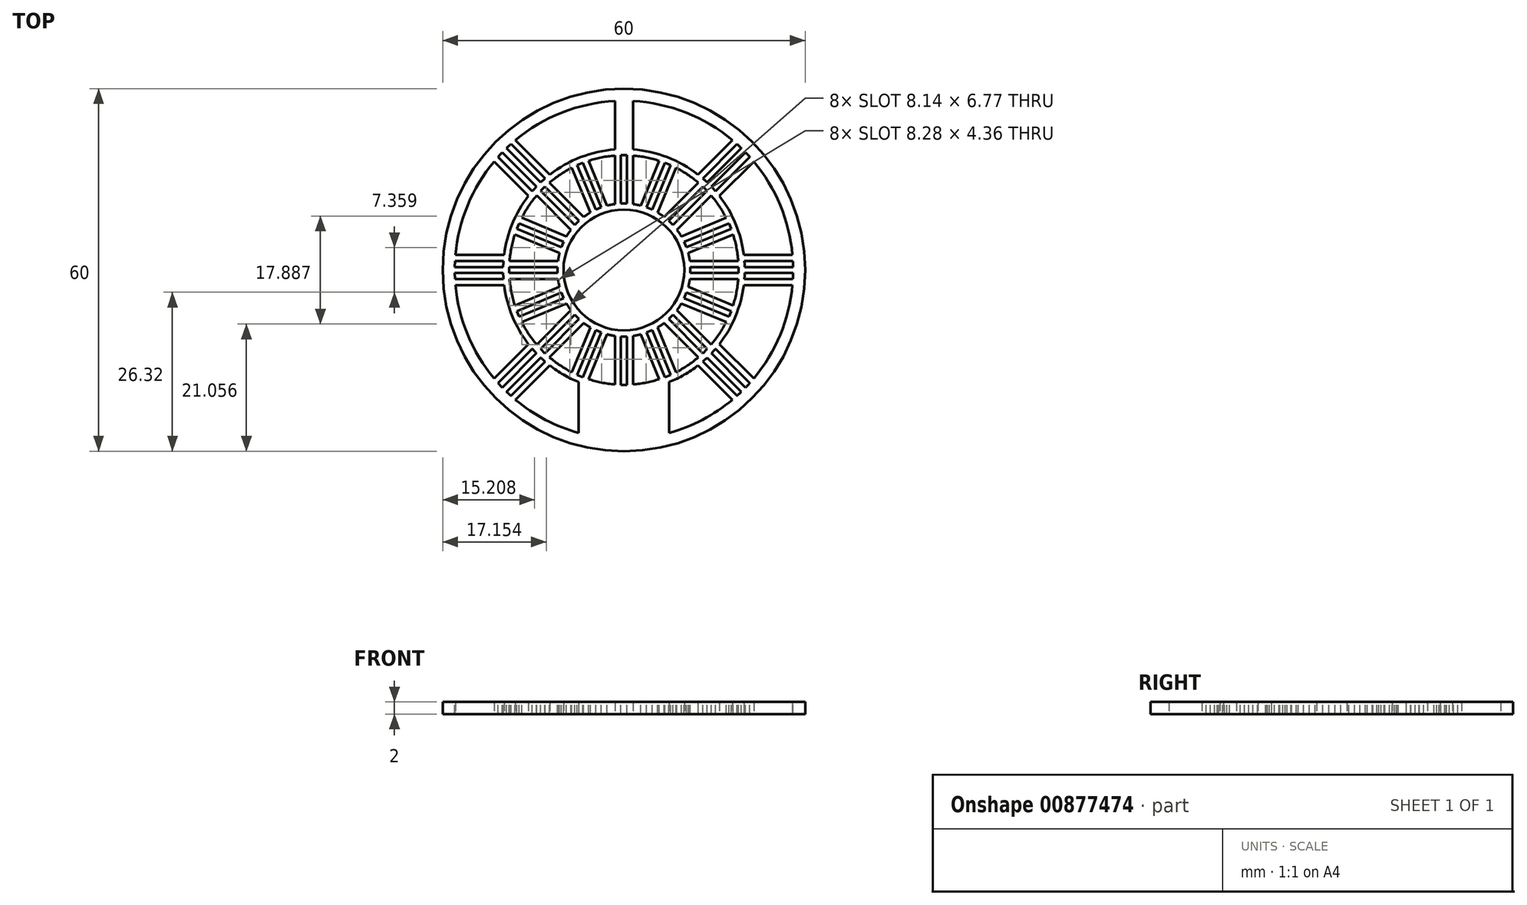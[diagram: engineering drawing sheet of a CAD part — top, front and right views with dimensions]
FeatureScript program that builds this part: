
annotation { "Feature Type Name" : "Feature", "Feature Type Description" : "" }
export const myFeature = defineFeature(function(context is Context, id is Id, definition is map)
    precondition{}
    {
        {
            var Q0;
            Q0=qCreatedBy(makeId("Top.planeOp"),FACE);
            var sketch = newSketch(context, id + "F0", { "sketchPlane" : qUnion([Q0])});
            skLineSegment(sketch, "E0", {"start": v(0, 41.56) * mm, "end": v(0, -42.56) * mm, "construction": true});
            skLineSegment(sketch, "E1", {"start": v(-1.5, 29.96) * mm, "end": v(-1.5, 19.94) * mm});
            skLineSegment(sketch, "E2.MirrorCS", {"start": v(1.5, 29.96) * mm, "end": v(1.5, 19.94) * mm});
            skCircle(sketch, "E3", {"center": v(0, 0) * mm, "radius": 10 * mm});
            skArc(sketch, "E4.trimOffspring", {"start": v(0, 30) * mm, "mid": v(-0.75, 30) * mm, "end": v(-1.5, 29.96) * mm});
            skArc(sketch, "E5", {"start": v(-1.5, 19.94) * mm, "mid": v(-7.19, 18.66) * mm, "end": v(-12.26, 15.8) * mm});
            skArc(sketch, "E6.trimOffspring", {"start": v(7.5, -18.54) * mm, "mid": v(9.98, -17.33) * mm, "end": v(12.26, -15.8) * mm});
            skLineSegment(sketch, "E7", {"start": v(-43.12, 0) * mm, "end": v(49.9, 0) * mm, "construction": true});
            skArc(sketch, "E8.trimOffspring", {"start": v(-19.6, -4) * mm, "mid": v(-18.17, -8.35) * mm, "end": v(-15.8, -12.26) * mm});
            skArc(sketch, "E9.trimOffspring", {"start": v(19.6, 4) * mm, "mid": v(18.17, 8.35) * mm, "end": v(15.8, 12.26) * mm});
            skArc(sketch, "E10", {"start": v(-19.6, 4) * mm, "mid": v(-19.73, 3.25) * mm, "end": v(-19.84, 2.5) * mm});
            skArc(sketch, "E11.trimOffspring", {"start": v(19.6, -4) * mm, "mid": v(19.73, -3.25) * mm, "end": v(19.84, -2.5) * mm});
            skLineSegment(sketch, "E12", {"start": v(-19.84, 2.5) * mm, "end": v(-29.9, 2.5) * mm});
            skLineSegment(sketch, "E13", {"start": v(-19.84, -2.5) * mm, "end": v(-29.9, -2.5) * mm});
            skArc(sketch, "E14.trimOffspring", {"start": v(-19.84, -2.5) * mm, "mid": v(-19.73, -3.25) * mm, "end": v(-19.6, -4) * mm});
            skLineSegment(sketch, "E15.MirrorCS", {"start": v(19.84, 2.5) * mm, "end": v(29.9, 2.5) * mm});
            skLineSegment(sketch, "E16.MirrorCS", {"start": v(19.84, -2.5) * mm, "end": v(29.9, -2.5) * mm});
            skArc(sketch, "E17.trimOffspring", {"start": v(19.84, 2.5) * mm, "mid": v(19.73, 3.25) * mm, "end": v(19.6, 4) * mm});
            skLineSegment(sketch, "E18", {"start": v(-7.5, -18.54) * mm, "end": v(-7.5, -29.05) * mm});
            skLineSegment(sketch, "E19", {"start": v(7.5, -18.54) * mm, "end": v(7.5, -29.05) * mm});
            skArc(sketch, "E20.trimOffspring", {"start": v(1.5, 29.96) * mm, "mid": v(0.75, 30) * mm, "end": v(0, 30) * mm});
            skPoint(sketch, "E21.orphan", {"position": v(29.9, 2.5) * mm});
            skPoint(sketch, "E22.MirrorCS.end.orphan", {"position": v(29.9, -2.5) * mm});
            skArc(sketch, "E23", {"start": v(-19.37, 22.9) * mm, "mid": v(-21.21, 21.21) * mm, "end": v(-22.9, 19.37) * mm});
            skLineSegment(sketch, "E24", {"start": v(-23.88, 23.88) * mm, "end": v(0, 0) * mm, "construction": true});
            skLineSegment(sketch, "E25", {"start": v(-12.26, 15.8) * mm, "end": v(-19.37, 22.9) * mm});
            skLineSegment(sketch, "E26", {"start": v(-15.8, 12.26) * mm, "end": v(-22.9, 19.37) * mm});
            skArc(sketch, "E27.trimOffspring", {"start": v(-29.9, 2.5) * mm, "mid": v(-30, 0) * mm, "end": v(-29.9, -2.5) * mm});
            skArc(sketch, "E28.trimOffspring", {"start": v(-7.5, -29.05) * mm, "mid": v(0, -30) * mm, "end": v(7.5, -29.05) * mm});
            skArc(sketch, "E29.trimOffspring", {"start": v(29.9, -2.5) * mm, "mid": v(30, 0) * mm, "end": v(29.9, 2.5) * mm});
            skArc(sketch, "E30.trimOffspring", {"start": v(1.5, 29.96) * mm, "mid": v(0, 30) * mm, "end": v(-1.5, 29.96) * mm});
            skArc(sketch, "E31.trimOffspring", {"start": v(-15.8, 12.26) * mm, "mid": v(-18.17, 8.35) * mm, "end": v(-19.6, 4) * mm});
            skLineSegment(sketch, "E32.MirrorCS", {"start": v(-15.8, -12.26) * mm, "end": v(-22.9, -19.37) * mm});
            skLineSegment(sketch, "E33.MirrorCS", {"start": v(-12.26, -15.8) * mm, "end": v(-19.37, -22.9) * mm});
            skArc(sketch, "E34.MirrorCS", {"start": v(-19.37, -22.9) * mm, "mid": v(-21.21, -21.21) * mm, "end": v(-22.9, -19.37) * mm});
            skArc(sketch, "E35.MirrorCS", {"start": v(19.37, 22.9) * mm, "mid": v(21.21, 21.21) * mm, "end": v(22.9, 19.37) * mm});
            skLineSegment(sketch, "E36.MirrorCS", {"start": v(12.26, 15.8) * mm, "end": v(19.37, 22.9) * mm});
            skLineSegment(sketch, "E37.MirrorCS", {"start": v(15.8, 12.26) * mm, "end": v(22.9, 19.37) * mm});
            skLineSegment(sketch, "E38.MirrorCS", {"start": v(15.8, -12.26) * mm, "end": v(22.9, -19.37) * mm});
            skArc(sketch, "E39.MirrorCS", {"start": v(19.37, -22.9) * mm, "mid": v(21.21, -21.21) * mm, "end": v(22.9, -19.37) * mm});
            skLineSegment(sketch, "E40.MirrorCS", {"start": v(12.26, -15.8) * mm, "end": v(19.37, -22.9) * mm});
            skArc(sketch, "E41.trimOffspring", {"start": v(12.26, 15.8) * mm, "mid": v(7.19, 18.66) * mm, "end": v(1.5, 19.94) * mm});
            skArc(sketch, "E42.trimOffspring", {"start": v(15.8, -12.26) * mm, "mid": v(18.17, -8.35) * mm, "end": v(19.6, -4) * mm});
            skArc(sketch, "E43.trimOffspring", {"start": v(-12.26, -15.8) * mm, "mid": v(-9.98, -17.33) * mm, "end": v(-7.5, -18.54) * mm});
            skSolve(sketch);
        }
        {
            var Q0;
            Q0=qSketchRegion(id+"F0",true);
            extrude(context, id + "F1", {"entities" : qUnion([Q0]), "depth" : 2 * mm, "offsetDistance" : 25 * mm});
        }
        {
            var Q0;
            Q0=makeQuery(id+"F1.opExtrude","CAP_FACE",FACE,{"disambiguationData":[OSD([sQuery(id+"F0.wireOp",EDGE,"E1"),sQuery(id+"F0.wireOp",EDGE,"E2.MirrorCS"),sQuery(id+"F0.wireOp",EDGE,"AAyOunAg-4wrl-KSGf-zJpX-W6BoPU9CkmaY"),sQuery(id+"F0.wireOp",EDGE,"E3"),sQuery(id+"F0.wireOp",EDGE,"E4.trimOffspring"),sQuery(id+"F0.wireOp",EDGE,"E5"),sQuery(id+"F0.wireOp",EDGE,"c113f9d6-7eb6-46a0-945d-8de39da3101e.trimOffspring"),sQuery(id+"F0.wireOp",EDGE,"3f556c1b-9434-4d6c-9e8b-53cfe23b14e8.trimOffspring"),sQuery(id+"F0.wireOp",EDGE,"E6.trimOffspring"),sQuery(id+"F0.wireOp",EDGE,"E8.trimOffspring"),sQuery(id+"F0.wireOp",EDGE,"E9.trimOffspring"),sQuery(id+"F0.wireOp",EDGE,"E10"),sQuery(id+"F0.wireOp",EDGE,"E11.trimOffspring")])],"isStart":false});
            var sketch = newSketch(context, id + "F2", { "sketchPlane" : qUnion([Q0])});
            skLineSegment(sketch, "E44", {"start": v(0, 19.87) * mm, "end": v(0, -17.42) * mm, "construction": true});
            skLineSegment(sketch, "E45", {"start": v(-0.5, 19) * mm, "end": v(-0.5, 11) * mm});
            skLineSegment(sketch, "E46", {"start": v(-0.5, 11) * mm, "end": v(0, 11) * mm});
            skLineSegment(sketch, "E47", {"start": v(-0.5, 19) * mm, "end": v(0, 19) * mm});
            skCircle(sketch, "E48", {"center": v(0, 0) * mm, "radius": 15 * mm, "construction": true});
            skLineSegment(sketch, "E49.MirrorCS", {"start": v(0.5, 19) * mm, "end": v(0, 19) * mm});
            skLineSegment(sketch, "E50.MirrorCS", {"start": v(0.5, 19) * mm, "end": v(0.5, 11) * mm});
            skLineSegment(sketch, "E51.MirrorCS", {"start": v(0.5, 11) * mm, "end": v(0, 11) * mm});
            skLineSegment(sketch, "E52.1.0", {"start": v(7.73, 17.36) * mm, "end": v(7.27, 17.55) * mm});
            skLineSegment(sketch, "E52.1.1", {"start": v(7.73, 17.36) * mm, "end": v(4.67, 9.97) * mm});
            skLineSegment(sketch, "E52.1.2", {"start": v(6.8, 17.75) * mm, "end": v(7.27, 17.55) * mm});
            skLineSegment(sketch, "E52.1.3", {"start": v(6.8, 17.75) * mm, "end": v(3.75, 10.35) * mm});
            skLineSegment(sketch, "E52.1.4", {"start": v(3.75, 10.35) * mm, "end": v(4.2, 10.16) * mm});
            skLineSegment(sketch, "E52.1.5", {"start": v(4.67, 9.97) * mm, "end": v(4.2, 10.16) * mm});
            skLineSegment(sketch, "E52.2.0", {"start": v(13.79, 13.08) * mm, "end": v(13.44, 13.44) * mm});
            skLineSegment(sketch, "E52.2.1", {"start": v(13.79, 13.08) * mm, "end": v(8.13, 7.42) * mm});
            skLineSegment(sketch, "E52.2.2", {"start": v(13.08, 13.79) * mm, "end": v(13.44, 13.44) * mm});
            skLineSegment(sketch, "E52.2.3", {"start": v(13.08, 13.79) * mm, "end": v(7.42, 8.13) * mm});
            skLineSegment(sketch, "E52.2.4", {"start": v(7.42, 8.13) * mm, "end": v(7.78, 7.78) * mm});
            skLineSegment(sketch, "E52.2.5", {"start": v(8.13, 7.42) * mm, "end": v(7.78, 7.78) * mm});
            skLineSegment(sketch, "E52.3.0", {"start": v(17.75, 6.8) * mm, "end": v(17.55, 7.27) * mm});
            skLineSegment(sketch, "E52.3.1", {"start": v(17.75, 6.8) * mm, "end": v(10.35, 3.75) * mm});
            skLineSegment(sketch, "E52.3.2", {"start": v(17.36, 7.73) * mm, "end": v(17.55, 7.27) * mm});
            skLineSegment(sketch, "E52.3.3", {"start": v(17.36, 7.73) * mm, "end": v(9.97, 4.67) * mm});
            skLineSegment(sketch, "E52.3.4", {"start": v(9.97, 4.67) * mm, "end": v(10.16, 4.2) * mm});
            skLineSegment(sketch, "E52.3.5", {"start": v(10.35, 3.75) * mm, "end": v(10.16, 4.2) * mm});
            skLineSegment(sketch, "E52.4.0", {"start": v(19, -0.5) * mm, "end": v(19, 0) * mm});
            skLineSegment(sketch, "E52.4.1", {"start": v(19, -0.5) * mm, "end": v(11, -0.5) * mm});
            skLineSegment(sketch, "E52.4.2", {"start": v(19, 0.5) * mm, "end": v(19, 0) * mm});
            skLineSegment(sketch, "E52.4.3", {"start": v(19, 0.5) * mm, "end": v(11, 0.5) * mm});
            skLineSegment(sketch, "E52.4.4", {"start": v(11, 0.5) * mm, "end": v(11, 0) * mm});
            skLineSegment(sketch, "E52.4.5", {"start": v(11, -0.5) * mm, "end": v(11, 0) * mm});
            skLineSegment(sketch, "E52.5.0", {"start": v(17.36, -7.73) * mm, "end": v(17.55, -7.27) * mm});
            skLineSegment(sketch, "E52.5.1", {"start": v(17.36, -7.73) * mm, "end": v(9.97, -4.67) * mm});
            skLineSegment(sketch, "E52.5.2", {"start": v(17.75, -6.8) * mm, "end": v(17.55, -7.27) * mm});
            skLineSegment(sketch, "E52.5.3", {"start": v(17.75, -6.8) * mm, "end": v(10.35, -3.75) * mm});
            skLineSegment(sketch, "E52.5.4", {"start": v(10.35, -3.75) * mm, "end": v(10.16, -4.2) * mm});
            skLineSegment(sketch, "E52.5.5", {"start": v(9.97, -4.67) * mm, "end": v(10.16, -4.2) * mm});
            skLineSegment(sketch, "E52.6.0", {"start": v(13.08, -13.79) * mm, "end": v(13.44, -13.44) * mm});
            skLineSegment(sketch, "E52.6.1", {"start": v(13.08, -13.79) * mm, "end": v(7.42, -8.13) * mm});
            skLineSegment(sketch, "E52.6.2", {"start": v(13.79, -13.08) * mm, "end": v(13.44, -13.44) * mm});
            skLineSegment(sketch, "E52.6.3", {"start": v(13.79, -13.08) * mm, "end": v(8.13, -7.42) * mm});
            skLineSegment(sketch, "E52.6.4", {"start": v(8.13, -7.42) * mm, "end": v(7.78, -7.78) * mm});
            skLineSegment(sketch, "E52.6.5", {"start": v(7.42, -8.13) * mm, "end": v(7.78, -7.78) * mm});
            skLineSegment(sketch, "E52.7.0", {"start": v(6.8, -17.75) * mm, "end": v(7.27, -17.55) * mm});
            skLineSegment(sketch, "E52.7.1", {"start": v(6.8, -17.75) * mm, "end": v(3.75, -10.35) * mm});
            skLineSegment(sketch, "E52.7.2", {"start": v(7.73, -17.36) * mm, "end": v(7.27, -17.55) * mm});
            skLineSegment(sketch, "E52.7.3", {"start": v(7.73, -17.36) * mm, "end": v(4.67, -9.97) * mm});
            skLineSegment(sketch, "E52.7.4", {"start": v(4.67, -9.97) * mm, "end": v(4.2, -10.16) * mm});
            skLineSegment(sketch, "E52.7.5", {"start": v(3.75, -10.35) * mm, "end": v(4.2, -10.16) * mm});
            skLineSegment(sketch, "E52.8.0", {"start": v(-0.5, -19) * mm, "end": v(0, -19) * mm});
            skLineSegment(sketch, "E52.8.1", {"start": v(-0.5, -19) * mm, "end": v(-0.5, -11) * mm});
            skLineSegment(sketch, "E52.8.2", {"start": v(0.5, -19) * mm, "end": v(0, -19) * mm});
            skLineSegment(sketch, "E52.8.3", {"start": v(0.5, -19) * mm, "end": v(0.5, -11) * mm});
            skLineSegment(sketch, "E52.8.4", {"start": v(0.5, -11) * mm, "end": v(0, -11) * mm});
            skLineSegment(sketch, "E52.8.5", {"start": v(-0.5, -11) * mm, "end": v(0, -11) * mm});
            skLineSegment(sketch, "E52.anchor1", {"start": v(0, 0) * mm, "end": v(0, 19) * mm, "construction": true});
            skLineSegment(sketch, "E52.anchor2", {"start": v(0, 0) * mm, "end": v(0, -19) * mm, "construction": true});
            skLineSegment(sketch, "E53.MirrorCS", {"start": v(-13.79, 13.08) * mm, "end": v(-13.44, 13.44) * mm});
            skLineSegment(sketch, "E54.MirrorCS", {"start": v(-19, 0.5) * mm, "end": v(-19, 0) * mm});
            skLineSegment(sketch, "E55.MirrorCS", {"start": v(-7.42, 8.13) * mm, "end": v(-7.78, 7.78) * mm});
            skLineSegment(sketch, "E56.MirrorCS", {"start": v(-17.75, -6.8) * mm, "end": v(-17.55, -7.27) * mm});
            skLineSegment(sketch, "E57.MirrorCS", {"start": v(-13.08, 13.79) * mm, "end": v(-13.44, 13.44) * mm});
            skLineSegment(sketch, "E58.MirrorCS", {"start": v(-8.13, -7.42) * mm, "end": v(-7.78, -7.78) * mm});
            skLineSegment(sketch, "E59.MirrorCS", {"start": v(-13.79, -13.08) * mm, "end": v(-13.44, -13.44) * mm});
            skLineSegment(sketch, "E60.MirrorCS", {"start": v(-17.75, 6.8) * mm, "end": v(-17.55, 7.27) * mm});
            skLineSegment(sketch, "E61.MirrorCS", {"start": v(-19, -0.5) * mm, "end": v(-19, 0) * mm});
            skLineSegment(sketch, "E62.MirrorCS", {"start": v(-13.08, -13.79) * mm, "end": v(-13.44, -13.44) * mm});
            skLineSegment(sketch, "E63.MirrorCS", {"start": v(-11, 0.5) * mm, "end": v(-11, 0) * mm});
            skLineSegment(sketch, "E64.MirrorCS", {"start": v(-6.8, -17.75) * mm, "end": v(-7.27, -17.55) * mm});
            skLineSegment(sketch, "E65.MirrorCS", {"start": v(-10.35, -3.75) * mm, "end": v(-10.16, -4.2) * mm});
            skLineSegment(sketch, "E66.MirrorCS", {"start": v(-7.73, 17.36) * mm, "end": v(-7.27, 17.55) * mm});
            skLineSegment(sketch, "E67.MirrorCS", {"start": v(-9.97, 4.67) * mm, "end": v(-10.16, 4.2) * mm});
            skLineSegment(sketch, "E68.MirrorCS", {"start": v(-9.97, -4.67) * mm, "end": v(-10.16, -4.2) * mm});
            skLineSegment(sketch, "E69.MirrorCS", {"start": v(-10.35, 3.75) * mm, "end": v(-10.16, 4.2) * mm});
            skLineSegment(sketch, "E70.MirrorCS", {"start": v(-7.73, -17.36) * mm, "end": v(-7.27, -17.55) * mm});
            skLineSegment(sketch, "E71.MirrorCS", {"start": v(-8.13, 7.42) * mm, "end": v(-7.78, 7.78) * mm});
            skLineSegment(sketch, "E72.MirrorCS", {"start": v(-7.42, -8.13) * mm, "end": v(-7.78, -7.78) * mm});
            skLineSegment(sketch, "E73.MirrorCS", {"start": v(-17.36, 7.73) * mm, "end": v(-17.55, 7.27) * mm});
            skLineSegment(sketch, "E74.MirrorCS", {"start": v(-11, -0.5) * mm, "end": v(-11, 0) * mm});
            skLineSegment(sketch, "E75.MirrorCS", {"start": v(-6.8, 17.75) * mm, "end": v(-7.27, 17.55) * mm});
            skLineSegment(sketch, "E76.MirrorCS", {"start": v(-17.36, -7.73) * mm, "end": v(-17.55, -7.27) * mm});
            skLineSegment(sketch, "E77.MirrorCS", {"start": v(-17.36, 7.73) * mm, "end": v(-9.97, 4.67) * mm});
            skLineSegment(sketch, "E78.MirrorCS", {"start": v(-13.79, -13.08) * mm, "end": v(-8.13, -7.42) * mm});
            skLineSegment(sketch, "E79.MirrorCS", {"start": v(-17.75, -6.8) * mm, "end": v(-10.35, -3.75) * mm});
            skLineSegment(sketch, "E80.MirrorCS", {"start": v(-19, 0.5) * mm, "end": v(-11, 0.5) * mm});
            skLineSegment(sketch, "E81.MirrorCS", {"start": v(-7.73, -17.36) * mm, "end": v(-4.67, -9.97) * mm});
            skLineSegment(sketch, "E82.MirrorCS", {"start": v(-17.75, 6.8) * mm, "end": v(-10.35, 3.75) * mm});
            skLineSegment(sketch, "E83.MirrorCS", {"start": v(-17.36, -7.73) * mm, "end": v(-9.97, -4.67) * mm});
            skLineSegment(sketch, "E84.MirrorCS", {"start": v(-7.73, 17.36) * mm, "end": v(-4.67, 9.97) * mm});
            skLineSegment(sketch, "E85.MirrorCS", {"start": v(-13.08, 13.79) * mm, "end": v(-7.42, 8.13) * mm});
            skLineSegment(sketch, "E86.MirrorCS", {"start": v(-19, -0.5) * mm, "end": v(-11, -0.5) * mm});
            skLineSegment(sketch, "E87.MirrorCS", {"start": v(-13.79, 13.08) * mm, "end": v(-8.13, 7.42) * mm});
            skLineSegment(sketch, "E88.MirrorCS", {"start": v(-13.08, -13.79) * mm, "end": v(-7.42, -8.13) * mm});
            skLineSegment(sketch, "E89.MirrorCS", {"start": v(-6.8, 17.75) * mm, "end": v(-3.75, 10.35) * mm});
            skLineSegment(sketch, "E90.MirrorCS", {"start": v(-3.75, 10.35) * mm, "end": v(-4.2, 10.16) * mm});
            skLineSegment(sketch, "E91.MirrorCS", {"start": v(-4.67, 9.97) * mm, "end": v(-4.2, 10.16) * mm});
            skLineSegment(sketch, "E92.MirrorCS", {"start": v(-3.75, -10.35) * mm, "end": v(-4.2, -10.16) * mm});
            skLineSegment(sketch, "E93.MirrorCS", {"start": v(-4.67, -9.97) * mm, "end": v(-4.2, -10.16) * mm});
            skLineSegment(sketch, "E94.MirrorCS", {"start": v(-6.8, -17.75) * mm, "end": v(-3.75, -10.35) * mm});
            skSolve(sketch);
        }
        {
            var Q0;
            Q0=qSketchRegion(id+"F2",true);
            extrude(context, id + "F3", {"entities" : qUnion([Q0]), "operationType" : NewBodyOperationType.REMOVE, "oppositeDirection" : true, "depth" : 25 * mm, "offsetDistance" : 25 * mm});
        }
        {
            var Q0;
            Q0=makeQuery(id+"F1.opExtrude","CAP_FACE",FACE,{"disambiguationData":[OSD([sQuery(id+"F0.wireOp",EDGE,"E1"),sQuery(id+"F0.wireOp",EDGE,"E2.MirrorCS"),sQuery(id+"F0.wireOp",EDGE,"AAyOunAg-4wrl-KSGf-zJpX-W6BoPU9CkmaY"),sQuery(id+"F0.wireOp",EDGE,"E3"),sQuery(id+"F0.wireOp",EDGE,"E4.trimOffspring"),sQuery(id+"F0.wireOp",EDGE,"E5"),sQuery(id+"F0.wireOp",EDGE,"c113f9d6-7eb6-46a0-945d-8de39da3101e.trimOffspring"),sQuery(id+"F0.wireOp",EDGE,"3f556c1b-9434-4d6c-9e8b-53cfe23b14e8.trimOffspring"),sQuery(id+"F0.wireOp",EDGE,"E6.trimOffspring"),sQuery(id+"F0.wireOp",EDGE,"E8.trimOffspring"),sQuery(id+"F0.wireOp",EDGE,"E9.trimOffspring"),sQuery(id+"F0.wireOp",EDGE,"E10"),sQuery(id+"F0.wireOp",EDGE,"E11.trimOffspring")])],"isStart":false});
            var sketch = newSketch(context, id + "F4", { "sketchPlane" : qUnion([Q0])});
            skArc(sketch, "E95", {"start": v(-1.5, 10.9) * mm, "mid": v(-2.15, 10.8) * mm, "end": v(-2.79, 10.65) * mm});
            skLineSegment(sketch, "E96", {"start": v(-1.5, 10.9) * mm, "end": v(-1.5, 18.93) * mm});
            skLineSegment(sketch, "E97", {"start": v(-2.79, 10.65) * mm, "end": v(-5.86, 18.07) * mm});
            skArc(sketch, "E98", {"start": v(-1.5, 18.93) * mm, "mid": v(-3.7, 18.63) * mm, "end": v(-5.86, 18.07) * mm});
            skArc(sketch, "E99.1.0", {"start": v(5.86, 18.07) * mm, "mid": v(3.7, 18.63) * mm, "end": v(1.5, 18.93) * mm});
            skLineSegment(sketch, "E99.1.1", {"start": v(2.79, 10.65) * mm, "end": v(5.86, 18.07) * mm});
            skArc(sketch, "E99.1.2", {"start": v(2.79, 10.65) * mm, "mid": v(2.15, 10.8) * mm, "end": v(1.5, 10.9) * mm});
            skLineSegment(sketch, "E99.1.3", {"start": v(1.5, 10.9) * mm, "end": v(1.5, 18.93) * mm});
            skArc(sketch, "E99.2.0", {"start": v(12.33, 14.45) * mm, "mid": v(10.55, 15.8) * mm, "end": v(8.63, 16.92) * mm});
            skLineSegment(sketch, "E99.2.1", {"start": v(6.65, 8.77) * mm, "end": v(12.33, 14.45) * mm});
            skArc(sketch, "E99.2.2", {"start": v(6.65, 8.77) * mm, "mid": v(6.12, 9.16) * mm, "end": v(5.56, 9.5) * mm});
            skLineSegment(sketch, "E99.2.3", {"start": v(5.56, 9.5) * mm, "end": v(8.63, 16.92) * mm});
            skArc(sketch, "E99.3.0", {"start": v(16.92, 8.63) * mm, "mid": v(15.8, 10.55) * mm, "end": v(14.45, 12.33) * mm});
            skLineSegment(sketch, "E99.3.1", {"start": v(9.5, 5.56) * mm, "end": v(16.92, 8.63) * mm});
            skArc(sketch, "E99.3.2", {"start": v(9.5, 5.56) * mm, "mid": v(9.16, 6.12) * mm, "end": v(8.77, 6.65) * mm});
            skLineSegment(sketch, "E99.3.3", {"start": v(8.77, 6.65) * mm, "end": v(14.45, 12.33) * mm});
            skArc(sketch, "E99.4.0", {"start": v(18.93, 1.5) * mm, "mid": v(18.63, 3.7) * mm, "end": v(18.07, 5.86) * mm});
            skLineSegment(sketch, "E99.4.1", {"start": v(10.9, 1.5) * mm, "end": v(18.93, 1.5) * mm});
            skArc(sketch, "E99.4.2", {"start": v(10.9, 1.5) * mm, "mid": v(10.8, 2.15) * mm, "end": v(10.65, 2.79) * mm});
            skLineSegment(sketch, "E99.4.3", {"start": v(10.65, 2.79) * mm, "end": v(18.07, 5.86) * mm});
            skArc(sketch, "E99.5.0", {"start": v(18.07, -5.86) * mm, "mid": v(18.63, -3.7) * mm, "end": v(18.93, -1.5) * mm});
            skLineSegment(sketch, "E99.5.1", {"start": v(10.65, -2.79) * mm, "end": v(18.07, -5.86) * mm});
            skArc(sketch, "E99.5.2", {"start": v(10.65, -2.79) * mm, "mid": v(10.8, -2.15) * mm, "end": v(10.9, -1.5) * mm});
            skLineSegment(sketch, "E99.5.3", {"start": v(10.9, -1.5) * mm, "end": v(18.93, -1.5) * mm});
            skArc(sketch, "E99.6.0", {"start": v(14.45, -12.33) * mm, "mid": v(15.8, -10.55) * mm, "end": v(16.92, -8.63) * mm});
            skLineSegment(sketch, "E99.6.1", {"start": v(8.77, -6.65) * mm, "end": v(14.45, -12.33) * mm});
            skArc(sketch, "E99.6.2", {"start": v(8.77, -6.65) * mm, "mid": v(9.16, -6.12) * mm, "end": v(9.5, -5.56) * mm});
            skLineSegment(sketch, "E99.6.3", {"start": v(9.5, -5.56) * mm, "end": v(16.92, -8.63) * mm});
            skArc(sketch, "E99.7.0", {"start": v(8.63, -16.92) * mm, "mid": v(10.55, -15.8) * mm, "end": v(12.33, -14.45) * mm});
            skLineSegment(sketch, "E99.7.1", {"start": v(5.56, -9.5) * mm, "end": v(8.63, -16.92) * mm});
            skArc(sketch, "E99.7.2", {"start": v(5.56, -9.5) * mm, "mid": v(6.12, -9.16) * mm, "end": v(6.65, -8.77) * mm});
            skLineSegment(sketch, "E99.7.3", {"start": v(6.65, -8.77) * mm, "end": v(12.33, -14.45) * mm});
            skArc(sketch, "E99.8.0", {"start": v(1.5, -18.93) * mm, "mid": v(3.7, -18.63) * mm, "end": v(5.86, -18.07) * mm});
            skLineSegment(sketch, "E99.8.1", {"start": v(1.5, -10.9) * mm, "end": v(1.5, -18.93) * mm});
            skArc(sketch, "E99.8.2", {"start": v(1.5, -10.9) * mm, "mid": v(2.15, -10.8) * mm, "end": v(2.79, -10.65) * mm});
            skLineSegment(sketch, "E99.8.3", {"start": v(2.79, -10.65) * mm, "end": v(5.86, -18.07) * mm});
            skLineSegment(sketch, "E99.anchor1", {"start": v(0, 0) * mm, "end": v(-5.86, 18.07) * mm, "construction": true});
            skLineSegment(sketch, "E99.anchor2", {"start": v(0, 0) * mm, "end": v(5.86, -18.07) * mm, "construction": true});
            skLineSegment(sketch, "E100", {"start": v(0, 24.57) * mm, "end": v(0, -24.9) * mm, "construction": true});
            skPoint(sketch, "E100.startSnap0", {"position": v(0, 23.23) * mm});
            skArc(sketch, "E101.MirrorCS", {"start": v(-12.33, 14.45) * mm, "mid": v(-10.55, 15.8) * mm, "end": v(-8.63, 16.92) * mm});
            skArc(sketch, "E102.MirrorCS", {"start": v(-10.9, 1.5) * mm, "mid": v(-10.8, 2.15) * mm, "end": v(-10.65, 2.79) * mm});
            skArc(sketch, "E103.MirrorCS", {"start": v(-8.77, -6.65) * mm, "mid": v(-9.16, -6.12) * mm, "end": v(-9.5, -5.56) * mm});
            skArc(sketch, "E104.MirrorCS", {"start": v(-10.65, -2.79) * mm, "mid": v(-10.8, -2.15) * mm, "end": v(-10.9, -1.5) * mm});
            skArc(sketch, "E105.MirrorCS", {"start": v(-9.5, 5.56) * mm, "mid": v(-9.16, 6.12) * mm, "end": v(-8.77, 6.65) * mm});
            skLineSegment(sketch, "E106.MirrorCS", {"start": v(-10.9, 1.5) * mm, "end": v(-18.93, 1.5) * mm});
            skLineSegment(sketch, "E107.MirrorCS", {"start": v(-8.77, -6.65) * mm, "end": v(-14.45, -12.33) * mm});
            skLineSegment(sketch, "E108.MirrorCS", {"start": v(-9.5, -5.56) * mm, "end": v(-16.92, -8.63) * mm});
            skArc(sketch, "E109.MirrorCS", {"start": v(-8.63, -16.92) * mm, "mid": v(-10.55, -15.8) * mm, "end": v(-12.33, -14.45) * mm});
            skArc(sketch, "E110.MirrorCS", {"start": v(-16.92, 8.63) * mm, "mid": v(-15.8, 10.55) * mm, "end": v(-14.45, 12.33) * mm});
            skLineSegment(sketch, "E111.MirrorCS", {"start": v(-10.65, -2.79) * mm, "end": v(-18.07, -5.86) * mm});
            skArc(sketch, "E112.MirrorCS", {"start": v(-14.45, -12.33) * mm, "mid": v(-15.8, -10.55) * mm, "end": v(-16.92, -8.63) * mm});
            skArc(sketch, "E113.MirrorCS", {"start": v(-18.93, 1.5) * mm, "mid": v(-18.63, 3.7) * mm, "end": v(-18.07, 5.86) * mm});
            skLineSegment(sketch, "E114.MirrorCS", {"start": v(-8.77, 6.65) * mm, "end": v(-14.45, 12.33) * mm});
            skLineSegment(sketch, "E115.MirrorCS", {"start": v(-10.65, 2.79) * mm, "end": v(-18.07, 5.86) * mm});
            skLineSegment(sketch, "E116.MirrorCS", {"start": v(-10.9, -1.5) * mm, "end": v(-18.93, -1.5) * mm});
            skLineSegment(sketch, "E117.MirrorCS", {"start": v(-9.5, 5.56) * mm, "end": v(-16.92, 8.63) * mm});
            skArc(sketch, "E118.MirrorCS", {"start": v(-18.07, -5.86) * mm, "mid": v(-18.63, -3.7) * mm, "end": v(-18.93, -1.5) * mm});
            skLineSegment(sketch, "E119.MirrorCS", {"start": v(-5.56, 9.5) * mm, "end": v(-8.63, 16.92) * mm});
            skLineSegment(sketch, "E120.MirrorCS", {"start": v(-6.65, 8.77) * mm, "end": v(-12.33, 14.45) * mm});
            skArc(sketch, "E121.MirrorCS", {"start": v(-6.65, 8.77) * mm, "mid": v(-6.12, 9.16) * mm, "end": v(-5.56, 9.5) * mm});
            skArc(sketch, "E122.MirrorCS", {"start": v(-5.56, -9.5) * mm, "mid": v(-6.12, -9.16) * mm, "end": v(-6.65, -8.77) * mm});
            skLineSegment(sketch, "E123.MirrorCS", {"start": v(-6.65, -8.77) * mm, "end": v(-12.33, -14.45) * mm});
            skLineSegment(sketch, "E124.MirrorCS", {"start": v(-5.56, -9.5) * mm, "end": v(-8.63, -16.92) * mm});
            skLineSegment(sketch, "E125.MirrorCS", {"start": v(-2.79, -10.65) * mm, "end": v(-5.86, -18.07) * mm});
            skArc(sketch, "E126.MirrorCS", {"start": v(-1.5, -10.9) * mm, "mid": v(-2.15, -10.8) * mm, "end": v(-2.79, -10.65) * mm});
            skLineSegment(sketch, "E127.MirrorCS", {"start": v(-1.5, -10.9) * mm, "end": v(-1.5, -18.93) * mm});
            skArc(sketch, "E128.MirrorCS", {"start": v(-1.5, -18.93) * mm, "mid": v(-3.7, -18.63) * mm, "end": v(-5.86, -18.07) * mm});
            skSolve(sketch);
        }
        {
            var Q0;
            Q0=qSketchRegion(id+"F4",true);
            extrude(context, id + "F5", {"entities" : qUnion([Q0]), "operationType" : NewBodyOperationType.REMOVE, "oppositeDirection" : true, "depth" : 25 * mm, "offsetDistance" : 25 * mm});
        }
        {
            var Q0;
            Q0=qCreatedBy(makeId("Top.planeOp"),FACE);
            var sketch = newSketch(context, id + "F6", { "sketchPlane" : qUnion([Q0])});
            skCircle(sketch, "E129", {"center": v(0, 0) * mm, "radius": 30 * mm});
            skCircle(sketch, "E130.0", {"center": v(0, 0) * mm, "radius": 28 * mm});
            skSolve(sketch);
        }
        {
            var Q0;
            Q0=qSketchRegion(id+"F6",true);
            extrude(context, id + "F7", {"entities" : qUnion([Q0]), "operationType" : NewBodyOperationType.ADD, "depth" : 2 * mm, "offsetDistance" : 25 * mm});
        }
        {
            var Q0;
            Q0=makeQuery(id+"F7.boolean.opBoolean","MERGE",FACE,{"derivedFrom":[makeQuery(id+"F1.opExtrude","CAP_FACE",FACE,{"disambiguationData":[OSD([sQuery(id+"F0.wireOp",EDGE,"E1"),sQuery(id+"F0.wireOp",EDGE,"E2.MirrorCS"),sQuery(id+"F0.wireOp",EDGE,"AAyOunAg-4wrl-KSGf-zJpX-W6BoPU9CkmaY"),sQuery(id+"F0.wireOp",EDGE,"E3"),sQuery(id+"F0.wireOp",EDGE,"E4.trimOffspring"),sQuery(id+"F0.wireOp",EDGE,"E5"),sQuery(id+"F0.wireOp",EDGE,"c113f9d6-7eb6-46a0-945d-8de39da3101e.trimOffspring"),sQuery(id+"F0.wireOp",EDGE,"3f556c1b-9434-4d6c-9e8b-53cfe23b14e8.trimOffspring"),sQuery(id+"F0.wireOp",EDGE,"E6.trimOffspring"),sQuery(id+"F0.wireOp",EDGE,"E8.trimOffspring"),sQuery(id+"F0.wireOp",EDGE,"E9.trimOffspring"),sQuery(id+"F0.wireOp",EDGE,"E10"),sQuery(id+"F0.wireOp",EDGE,"E11.trimOffspring"),sQuery(id+"F0.wireOp",EDGE,"E12"),sQuery(id+"F0.wireOp",EDGE,"kXOEPWS2-C3rD-1ilS-GXDP-zmpu0qmiIk17"),sQuery(id+"F0.wireOp",EDGE,"ba19601d-0a29-4faa-a46e-a923055b0abc.trimOffspring"),sQuery(id+"F0.wireOp",EDGE,"E13"),sQuery(id+"F0.wireOp",EDGE,"E14.trimOffspring"),sQuery(id+"F0.wireOp",EDGE,"E15.MirrorCS"),sQuery(id+"F0.wireOp",EDGE,"E22.MirrorCS"),sQuery(id+"F0.wireOp",EDGE,"E16.MirrorCS"),sQuery(id+"F0.wireOp",EDGE,"E17.trimOffspring")])],"isStart":false}),makeQuery(id+"F7.opExtrude","CAP_FACE",FACE,{"disambiguationData":[OSD([sQuery(id+"F6.wireOp",EDGE,"E129"),sQuery(id+"F6.wireOp",EDGE,"E130.0")])],"isStart":false})]});
            var sketch = newSketch(context, id + "F8", { "sketchPlane" : qUnion([Q0])});
            skLineSegment(sketch, "E131.1.0", {"start": v(-19.94, 1.5) * mm, "end": v(-27.96, 1.5) * mm});
            skLineSegment(sketch, "E131.1.1", {"start": v(-20, 0.5) * mm, "end": v(-28, 0.5) * mm});
            skArc(sketch, "E131.1.2", {"start": v(-20, -0.5) * mm, "mid": v(-19.97, -1) * mm, "end": v(-19.94, -1.5) * mm});
            skArc(sketch, "E131.1.3", {"start": v(-28, -0.5) * mm, "mid": v(-27.98, -1) * mm, "end": v(-27.96, -1.5) * mm});
            skLineSegment(sketch, "E131.1.4", {"start": v(-20, -0.5) * mm, "end": v(-28, -0.5) * mm});
            skArc(sketch, "E131.1.5", {"start": v(-19.94, 1.5) * mm, "mid": v(-19.97, 1) * mm, "end": v(-20, 0.5) * mm});
            skPoint(sketch, "E131.1.6", {"position": v(-19.94, 1.5) * mm});
            skLineSegment(sketch, "E131.1.7", {"start": v(-19.94, -1.5) * mm, "end": v(-27.96, -1.5) * mm});
            skArc(sketch, "E131.1.8", {"start": v(-27.96, 1.5) * mm, "mid": v(-27.98, 1) * mm, "end": v(-28, 0.5) * mm});
            skPoint(sketch, "E131.center", {"position": v(0, 0) * mm});
            skLineSegment(sketch, "E132", {"start": v(0, -35.42) * mm, "end": v(0, 33.86) * mm, "construction": true});
            skArc(sketch, "E133.MirrorCS", {"start": v(19.94, 1.5) * mm, "mid": v(19.97, 1) * mm, "end": v(20, 0.5) * mm});
            skArc(sketch, "E134.MirrorCS", {"start": v(20, -0.5) * mm, "mid": v(19.97, -1) * mm, "end": v(19.94, -1.5) * mm});
            skArc(sketch, "E135.MirrorCS", {"start": v(27.96, 1.5) * mm, "mid": v(27.98, 1) * mm, "end": v(28, 0.5) * mm});
            skArc(sketch, "E136.MirrorCS", {"start": v(28, -0.5) * mm, "mid": v(27.98, -1) * mm, "end": v(27.96, -1.5) * mm});
            skPoint(sketch, "E137.MirrorP", {"position": v(19.94, 1.5) * mm});
            skLineSegment(sketch, "E138.MirrorCS", {"start": v(19.94, 1.5) * mm, "end": v(27.96, 1.5) * mm});
            skLineSegment(sketch, "E139.MirrorCS", {"start": v(19.94, -1.5) * mm, "end": v(27.96, -1.5) * mm});
            skLineSegment(sketch, "E140.MirrorCS", {"start": v(20, -0.5) * mm, "end": v(28, -0.5) * mm});
            skLineSegment(sketch, "E141.MirrorCS", {"start": v(20, 0.5) * mm, "end": v(28, 0.5) * mm});
            skLineSegment(sketch, "E142.1.0", {"start": v(-14.5, 13.78) * mm, "end": v(-20.15, 19.44) * mm});
            skLineSegment(sketch, "E142.1.1", {"start": v(-13.04, 15.16) * mm, "end": v(-18.7, 20.83) * mm});
            skPoint(sketch, "E142.1.2", {"position": v(-13.04, 15.16) * mm});
            skLineSegment(sketch, "E142.1.3", {"start": v(-13.78, 14.5) * mm, "end": v(-19.44, 20.15) * mm});
            skLineSegment(sketch, "E142.1.4", {"start": v(-15.16, 13.04) * mm, "end": v(-20.83, 18.7) * mm});
            skArc(sketch, "E142.1.5", {"start": v(-18.7, 20.83) * mm, "mid": v(-19.08, 20.5) * mm, "end": v(-19.44, 20.15) * mm});
            skArc(sketch, "E142.1.6", {"start": v(-20.15, 19.44) * mm, "mid": v(-20.5, 19.08) * mm, "end": v(-20.83, 18.7) * mm});
            skArc(sketch, "E142.1.7", {"start": v(-13.04, 15.16) * mm, "mid": v(-13.42, 14.83) * mm, "end": v(-13.78, 14.5) * mm});
            skArc(sketch, "E142.1.8", {"start": v(-14.5, 13.78) * mm, "mid": v(-14.83, 13.42) * mm, "end": v(-15.16, 13.04) * mm});
            skLineSegment(sketch, "E143", {"start": v(-33.35, 0) * mm, "end": v(38.88, 0) * mm, "construction": true});
            skArc(sketch, "E144.MirrorCS", {"start": v(-13.04, -15.16) * mm, "mid": v(-13.42, -14.83) * mm, "end": v(-13.78, -14.5) * mm});
            skArc(sketch, "E145.MirrorCS", {"start": v(-14.5, -13.78) * mm, "mid": v(-14.83, -13.42) * mm, "end": v(-15.16, -13.04) * mm});
            skArc(sketch, "E146.MirrorCS", {"start": v(-20.15, -19.44) * mm, "mid": v(-20.5, -19.08) * mm, "end": v(-20.83, -18.7) * mm});
            skArc(sketch, "E147.MirrorCS", {"start": v(-18.7, -20.83) * mm, "mid": v(-19.08, -20.5) * mm, "end": v(-19.44, -20.15) * mm});
            skPoint(sketch, "E148.MirrorP", {"position": v(-13.04, -15.16) * mm});
            skLineSegment(sketch, "E149.MirrorCS", {"start": v(-13.78, -14.5) * mm, "end": v(-19.44, -20.15) * mm});
            skLineSegment(sketch, "E150.MirrorCS", {"start": v(-15.16, -13.04) * mm, "end": v(-20.83, -18.7) * mm});
            skLineSegment(sketch, "E151.MirrorCS", {"start": v(-14.5, -13.78) * mm, "end": v(-20.15, -19.44) * mm});
            skLineSegment(sketch, "E152.MirrorCS", {"start": v(-13.04, -15.16) * mm, "end": v(-18.7, -20.83) * mm});
            skArc(sketch, "E153.MirrorCS", {"start": v(13.04, 15.16) * mm, "mid": v(13.42, 14.83) * mm, "end": v(13.78, 14.5) * mm});
            skArc(sketch, "E154.MirrorCS", {"start": v(14.5, 13.78) * mm, "mid": v(14.83, 13.42) * mm, "end": v(15.16, 13.04) * mm});
            skArc(sketch, "E155.MirrorCS", {"start": v(18.7, 20.83) * mm, "mid": v(19.08, 20.5) * mm, "end": v(19.44, 20.15) * mm});
            skArc(sketch, "E156.MirrorCS", {"start": v(20.15, 19.44) * mm, "mid": v(20.5, 19.08) * mm, "end": v(20.83, 18.7) * mm});
            skLineSegment(sketch, "E157.MirrorCS", {"start": v(13.04, 15.16) * mm, "end": v(18.7, 20.83) * mm});
            skLineSegment(sketch, "E158.MirrorCS", {"start": v(14.5, 13.78) * mm, "end": v(20.15, 19.44) * mm});
            skLineSegment(sketch, "E159.MirrorCS", {"start": v(13.78, 14.5) * mm, "end": v(19.44, 20.15) * mm});
            skPoint(sketch, "E160.MirrorP", {"position": v(13.04, 15.16) * mm});
            skLineSegment(sketch, "E161.MirrorCS", {"start": v(15.16, 13.04) * mm, "end": v(20.83, 18.7) * mm});
            skArc(sketch, "E162.MirrorCS", {"start": v(13.04, -15.16) * mm, "mid": v(13.42, -14.83) * mm, "end": v(13.78, -14.5) * mm});
            skArc(sketch, "E163.MirrorCS", {"start": v(14.5, -13.78) * mm, "mid": v(14.83, -13.42) * mm, "end": v(15.16, -13.04) * mm});
            skArc(sketch, "E164.MirrorCS", {"start": v(18.7, -20.83) * mm, "mid": v(19.08, -20.5) * mm, "end": v(19.44, -20.15) * mm});
            skArc(sketch, "E165.MirrorCS", {"start": v(20.15, -19.44) * mm, "mid": v(20.5, -19.08) * mm, "end": v(20.83, -18.7) * mm});
            skLineSegment(sketch, "E166.MirrorCS", {"start": v(14.5, -13.78) * mm, "end": v(20.15, -19.44) * mm});
            skPoint(sketch, "E167.MirrorP", {"position": v(13.04, -15.16) * mm});
            skLineSegment(sketch, "E168.MirrorCS", {"start": v(13.04, -15.16) * mm, "end": v(18.7, -20.83) * mm});
            skLineSegment(sketch, "E169.MirrorCS", {"start": v(13.78, -14.5) * mm, "end": v(19.44, -20.15) * mm});
            skLineSegment(sketch, "E170.MirrorCS", {"start": v(15.16, -13.04) * mm, "end": v(20.83, -18.7) * mm});
            skSolve(sketch);
        }
        {
            var Q0;
            Q0 = qSketchRegion(id + "F8", true);
            extrude(context, id + "F9", {"entities" : qUnion([Q0]), "operationType" : NewBodyOperationType.REMOVE, "oppositeDirection" : true, "depth" : 25 * mm, "offsetDistance" : 25 * mm});
        }
    });
